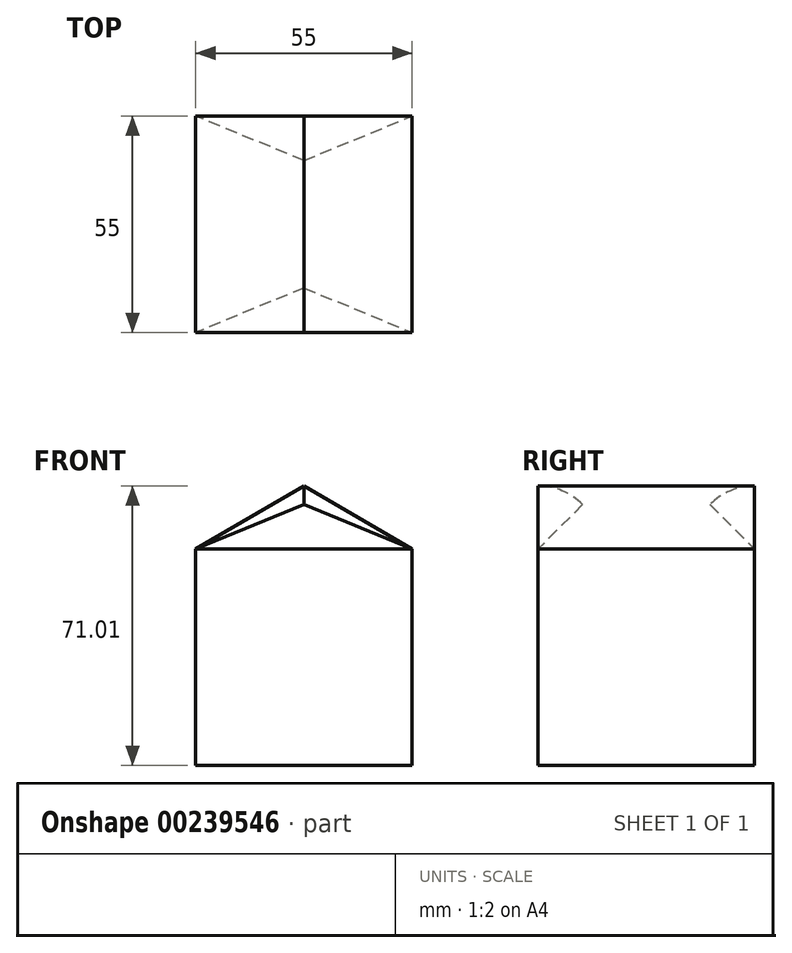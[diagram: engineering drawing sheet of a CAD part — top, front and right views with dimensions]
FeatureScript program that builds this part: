
annotation { "Feature Type Name" : "Feature", "Feature Type Description" : "" }
export const myFeature = defineFeature(function(context is Context, id is Id, definition is map)
    precondition{}
    {
        {
            var Q0;
            Q0=qCreatedBy(makeId("Front.planeOp"),FACE);
            var sketch = newSketch(context, id + "F0", { "sketchPlane" : qUnion([Q0])});
            skLineSegment(sketch, "E0.bottom", {"start": v(27.5, 27.5) * mm, "end": v(-27.5, 27.5) * mm});
            skLineSegment(sketch, "E0.top", {"start": v(27.5, -27.5) * mm, "end": v(-27.5, -27.5) * mm});
            skLineSegment(sketch, "E0.left", {"start": v(27.5, 27.5) * mm, "end": v(27.5, -27.5) * mm});
            skLineSegment(sketch, "E0.right", {"start": v(-27.5, 27.5) * mm, "end": v(-27.5, -27.5) * mm});
            skPoint(sketch, "E0.middle", {"position": v(0, 0) * mm});
            skSolve(sketch);
        }
        {
            var Q0;
            Q0 = qSketchRegion(id + "F0", true);
            extrude(context, id + "F1", {"entities" : qUnion([Q0]), "endBound" : BoundingType.SYMMETRIC, "depth" : 55 * mm});
        }
        {
            var Q0;
            Q0=qCreatedBy(makeId("Front.planeOp"),FACE);
            var sketch = newSketch(context, id + "F2", { "sketchPlane" : qUnion([Q0])});
            skLineSegment(sketch, "E1", {"start": v(0, 0) * mm, "end": v(0, 43.51) * mm, "construction": true});
            skSolve(sketch);
        }
        {
            var Q0;
            Q0=qCreatedBy(makeId("Front.planeOp"),FACE);
            var sketch = newSketch(context, id + "F3", { "sketchPlane" : qUnion([Q0])});
            skPoint(sketch, "E2.0", {"position": v(0, 43.51) * mm});
            skPoint(sketch, "E3.0", {"position": v(-27.5, 27.5) * mm});
            skLineSegment(sketch, "E4", {"start": v(0, 43.51) * mm, "end": v(-27.5, 27.5) * mm});
            skPoint(sketch, "E5.0", {"position": v(27.5, 27.5) * mm});
            skLineSegment(sketch, "E6", {"start": v(0, 43.51) * mm, "end": v(27.5, 27.5) * mm});
            skLineSegment(sketch, "E7", {"start": v(-27.5, 27.5) * mm, "end": v(27.5, 27.5) * mm});
            skSolve(sketch);
        }
        {
            var Q0;
            Q0=makeQuery(id+"F3.imprint","IMPRINT",FACE,{"disambiguationData":[TD([[makeQuery(id+"F3.imprint","IMPRINT",EDGE,{"derivedFrom":sQuery(id+"F3.wireOp",EDGE,"E4")}),1.0]])]});
            extrude(context, id + "F4", {"entities" : qUnion([Q0]), "operationType" : NewBodyOperationType.ADD, "endBound" : BoundingType.SYMMETRIC, "depth" : 55 * mm});
        }
        {
            var Q0;
            Q0=makeQuery(id+"F4.boolean.opBoolean","MERGE",FACE,{"derivedFrom":[makeQuery(id+"F1.opExtrude","CAP_FACE",FACE,{"disambiguationData":[OSD([sQuery(id+"F0.wireOp",EDGE,"E0.bottom"),sQuery(id+"F0.wireOp",EDGE,"E0.top"),sQuery(id+"F0.wireOp",EDGE,"E0.left"),sQuery(id+"F0.wireOp",EDGE,"E0.right")])],"isStart":false}),makeQuery(id+"F4.opExtrude","CAP_FACE",FACE,{"disambiguationData":[OSD([sQuery(id+"F3.wireOp",EDGE,"E4"),sQuery(id+"F3.wireOp",EDGE,"E6"),sQuery(id+"F3.wireOp",EDGE,"E7")])],"isStart":false})]});
            var sketch = newSketch(context, id + "F5", { "sketchPlane" : qUnion([Q0])});
            skPoint(sketch, "E8.0", {"position": v(0, 43.51) * mm});
            skPoint(sketch, "E9.0", {"position": v(-27.5, 27.5) * mm});
            skPoint(sketch, "E10.0", {"position": v(27.5, 27.5) * mm});
            skLineSegment(sketch, "E11", {"start": v(-27.5, 27.5) * mm, "end": v(27.5, 27.5) * mm});
            skLineSegment(sketch, "E12", {"start": v(0, 43.51) * mm, "end": v(-27.5, 27.5) * mm});
            skLineSegment(sketch, "E13", {"start": v(0, 43.51) * mm, "end": v(27.5, 27.5) * mm});
            skSolve(sketch);
        }
        {
            var Q0;
            Q0 = qSketchRegion(id + "F5", true);
            var Q1;
            Q1=sQuery(id+"F5.wireOp",EDGE,"E11");
            revolve(context, id + "F6", {"operationType" : NewBodyOperationType.REMOVE, "entities" : qUnion([Q0]), "axis" : qUnion([Q1]), "revolveType" : RevolveType.ONE_DIRECTION, "oppositeDirection" : true, "angle" : 45 * degree});
        }
        {
            var Q0;
            Q0=makeQuery(id+"F4.boolean.opBoolean","MERGE",FACE,{"derivedFrom":[makeQuery(id+"F1.opExtrude","CAP_FACE",FACE,{"disambiguationData":[OSD([sQuery(id+"F0.wireOp",EDGE,"E0.bottom"),sQuery(id+"F0.wireOp",EDGE,"E0.top"),sQuery(id+"F0.wireOp",EDGE,"E0.left"),sQuery(id+"F0.wireOp",EDGE,"E0.right")])],"isStart":true}),makeQuery(id+"F4.opExtrude","CAP_FACE",FACE,{"disambiguationData":[OSD([sQuery(id+"F3.wireOp",EDGE,"E4"),sQuery(id+"F3.wireOp",EDGE,"E6"),sQuery(id+"F3.wireOp",EDGE,"E7")])],"isStart":true})]});
            var sketch = newSketch(context, id + "F7", { "sketchPlane" : qUnion([Q0])});
            skPoint(sketch, "E14.0", {"position": v(0, 43.51) * mm});
            skPoint(sketch, "E15.0", {"position": v(-27.5, 27.5) * mm});
            skPoint(sketch, "E16.0", {"position": v(27.5, 27.5) * mm});
            skLineSegment(sketch, "E17", {"start": v(-27.5, 27.5) * mm, "end": v(27.5, 27.5) * mm});
            skLineSegment(sketch, "E18", {"start": v(0, 43.51) * mm, "end": v(-27.5, 27.5) * mm});
            skLineSegment(sketch, "E19", {"start": v(0, 43.51) * mm, "end": v(27.5, 27.5) * mm});
            skSolve(sketch);
        }
        {
            var Q0;
            Q0 = qSketchRegion(id + "F7", true);
            var Q1;
            Q1=sQuery(id+"F7.wireOp",EDGE,"E17");
            revolve(context, id + "F8", {"operationType" : NewBodyOperationType.REMOVE, "entities" : qUnion([Q0]), "axis" : qUnion([Q1]), "revolveType" : RevolveType.ONE_DIRECTION, "oppositeDirection" : true, "angle" : 45 * degree});
        }
    });
